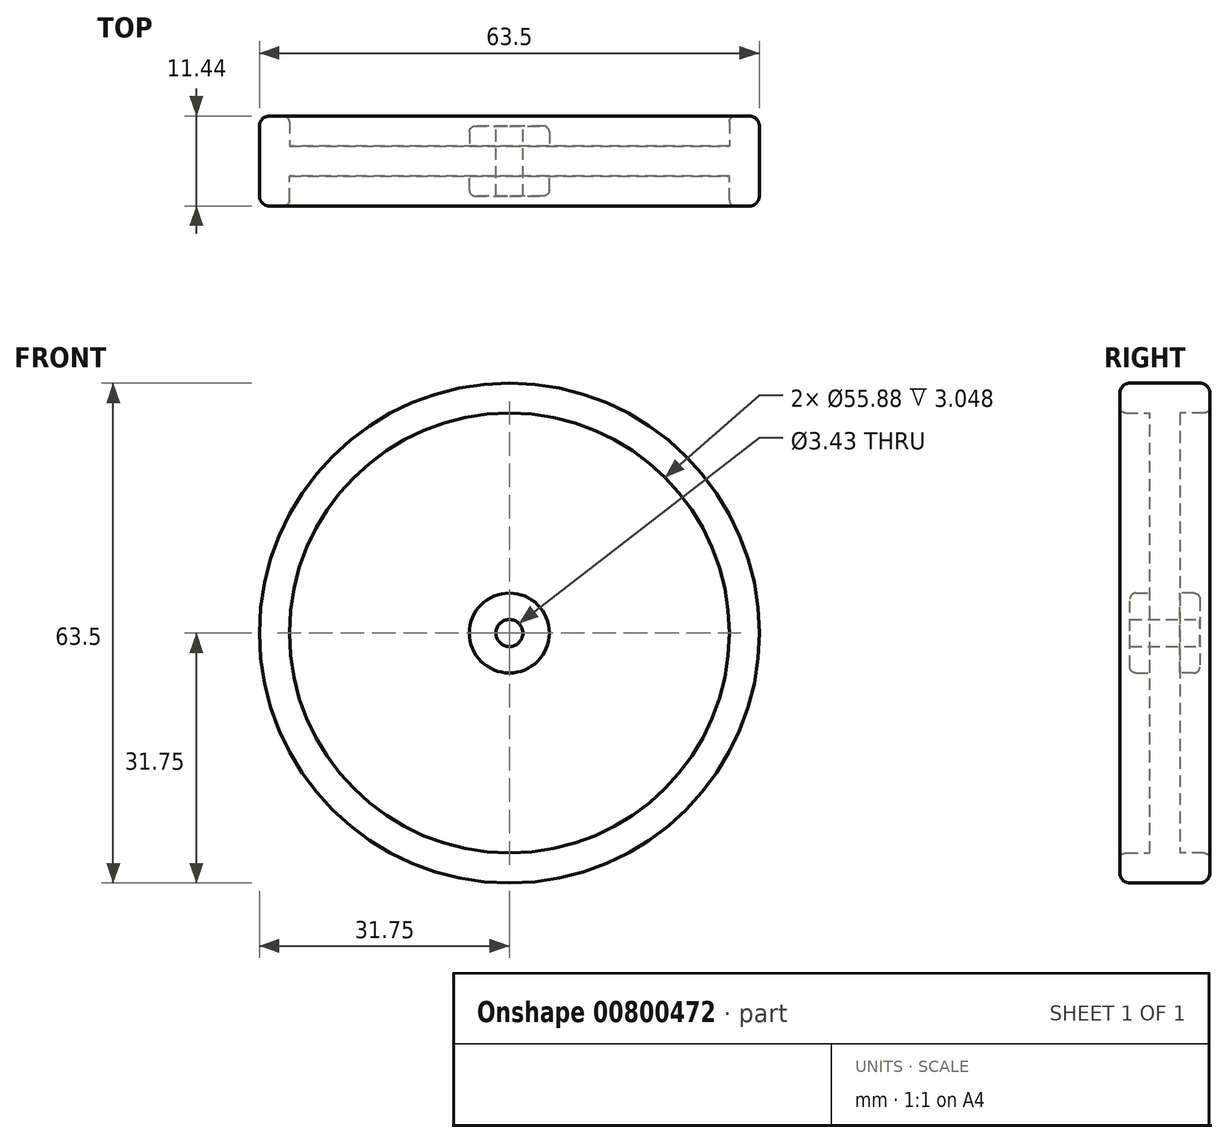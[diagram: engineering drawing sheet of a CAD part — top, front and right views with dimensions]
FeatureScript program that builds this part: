
annotation { "Feature Type Name" : "Feature", "Feature Type Description" : "" }
export const myFeature = defineFeature(function(context is Context, id is Id, definition is map)
    precondition{}
    {
        {
            var Q0;
            Q0=qCreatedBy(makeId("Front.planeOp"),FACE);
            var sketch = newSketch(context, id + "F0", { "sketchPlane" : qUnion([Q0])});
            skCircle(sketch, "E0", {"center": v(0, 0) * mm, "radius": 31.75 * mm});
            skCircle(sketch, "E1", {"center": v(0, 0) * mm, "radius": 1.71 * mm});
            skCircle(sketch, "E2", {"center": v(0, 0) * mm, "radius": 25.4 * mm});
            skSolve(sketch);
        }
        {
            var Q0;
            Q0=makeQuery(id+"F0.imprint","IMPRINT",FACE,{"disambiguationData":[TD([[makeQuery(id+"F0.imprint","IMPRINT",EDGE,{"derivedFrom":sQuery(id+"F0.wireOp",EDGE,"E0")}),1.0]])]});
            var Q1;
            Q1=makeQuery(id+"F0.imprint","IMPRINT",FACE,{"disambiguationData":[TD([[makeQuery(id+"F0.imprint","IMPRINT",EDGE,{"derivedFrom":sQuery(id+"F0.wireOp",EDGE,"E1")}),-1.0]])]});
            extrude(context, id + "F1", {"entities" : qUnion([Q0, Q1]), "endBound" : BoundingType.SYMMETRIC, "depth" : 3.8 * mm, "offsetDistance" : 25.4 * mm});
        }
        {
            var Q0;
            Q0=makeQuery(id+"F1.opExtrude","CAP_FACE",FACE,{"disambiguationData":[OSD([sQuery(id+"F0.wireOp",EDGE,"E0"),sQuery(id+"F0.wireOp",EDGE,"E1")])],"isStart":false});
            var sketch = newSketch(context, id + "F2", { "sketchPlane" : qUnion([Q0])});
            skCircle(sketch, "E3", {"center": v(0, 0) * mm, "radius": 27.94 * mm});
            skSolve(sketch);
        }
        {
            var Q0;
            Q0=makeQuery(id+"F2.imprint","IMPRINT",FACE,{"disambiguationData":[TD([[makeQuery(id+"F2.imprint","IMPRINT",EDGE,{"derivedFrom":sQuery(id+"F2.wireOp",EDGE,"E3")}),-1.0]])]});
            extrude(context, id + "F3", {"entities" : qUnion([Q0]), "operationType" : NewBodyOperationType.ADD, "depth" : 3.8 * mm, "offsetDistance" : 25.4 * mm});
        }
        {
            var Q0;
            Q0=makeQuery(id+"F1.opExtrude","CAP_FACE",FACE,{"disambiguationData":[OSD([sQuery(id+"F0.wireOp",EDGE,"E0"),sQuery(id+"F0.wireOp",EDGE,"E1")])],"isStart":true});
            var sketch = newSketch(context, id + "F4", { "sketchPlane" : qUnion([Q0])});
            skCircle(sketch, "E4", {"center": v(0, 0) * mm, "radius": 27.94 * mm});
            skSolve(sketch);
        }
        {
            var Q0;
            Q0=makeQuery(id+"F4.imprint","IMPRINT",FACE,{"disambiguationData":[TD([[makeQuery(id+"F4.imprint","IMPRINT",EDGE,{"derivedFrom":sQuery(id+"F4.wireOp",EDGE,"E4")}),-1.0]])]});
            extrude(context, id + "F5", {"entities" : qUnion([Q0]), "operationType" : NewBodyOperationType.ADD, "depth" : 3.8 * mm, "offsetDistance" : 25.4 * mm});
        }
        {
            var Q0;
            Q0=makeQuery(id+"F1.opExtrude","CAP_FACE",FACE,{"disambiguationData":[OSD([sQuery(id+"F0.wireOp",EDGE,"E0"),sQuery(id+"F0.wireOp",EDGE,"E1")])],"isStart":false});
            var sketch = newSketch(context, id + "F6", { "sketchPlane" : qUnion([Q0])});
            skCircle(sketch, "E5", {"center": v(0, 0) * mm, "radius": 5.08 * mm});
            skSolve(sketch);
        }
        {
            var Q0;
            Q0=makeQuery(id+"F6.imprint","IMPRINT",FACE,{"disambiguationData":[TD([[makeQuery(id+"F6.imprint","IMPRINT",EDGE,{"derivedFrom":sQuery(id+"F6.wireOp",EDGE,"E5")}),1.0]])]});
            extrude(context, id + "F7", {"entities" : qUnion([Q0]), "operationType" : NewBodyOperationType.ADD, "depth" : 2.54 * mm, "offsetDistance" : 25.4 * mm});
        }
        {
            var Q0;
            Q0=makeQuery(id+"F1.opExtrude","CAP_FACE",FACE,{"disambiguationData":[OSD([sQuery(id+"F0.wireOp",EDGE,"E0"),sQuery(id+"F0.wireOp",EDGE,"E1")])],"isStart":true});
            var sketch = newSketch(context, id + "F8", { "sketchPlane" : qUnion([Q0])});
            skCircle(sketch, "E6", {"center": v(0, 0) * mm, "radius": 5.08 * mm});
            skSolve(sketch);
        }
        {
            var Q0;
            Q0=makeQuery(id+"F8.imprint","IMPRINT",FACE,{"disambiguationData":[TD([[makeQuery(id+"F8.imprint","IMPRINT",EDGE,{"derivedFrom":sQuery(id+"F8.wireOp",EDGE,"E6")}),1.0]])]});
            extrude(context, id + "F9", {"entities" : qUnion([Q0]), "operationType" : NewBodyOperationType.ADD, "depth" : 2.54 * mm, "offsetDistance" : 25.4 * mm});
        }
        {
            var Q0;
            Q0=makeQuery(id+"F5.opExtrude","CAP_EDGE",EDGE,{"disambiguationData":[OSD([sQuery(id+"F4.wireOp",EDGE,"E4")])],"isStart":false});
            var Q1;
            Q1=makeQuery(id+"F3.opExtrude","CAP_EDGE",EDGE,{"disambiguationData":[OSD([sQuery(id+"F2.wireOp",EDGE,"E3")])],"isStart":false});
            var Q2;
            Q2=makeQuery(id+"F9.opExtrude","CAP_EDGE",EDGE,{"disambiguationData":[OSD([sQuery(id+"F8.wireOp",EDGE,"E6")])],"isStart":false});
            var Q3;
            Q3=makeQuery(id+"F7.opExtrude","CAP_EDGE",EDGE,{"disambiguationData":[OSD([sQuery(id+"F6.wireOp",EDGE,"E5")])],"isStart":false});
            fillet(context, id + "F10", {"entities" : qUnion([Q0, Q1, Q2, Q3]), "radius" : 0.76 * mm, "tangentPropagation" : true, "allowEdgeOverflow" : false});
        }
        {
            var Q0;
            Q0=makeQuery(id+"F3.opExtrude","CAP_EDGE",EDGE,{"disambiguationData":[OSD([sQuery(id+"F0.wireOp",EDGE,"E0")])],"isStart":false});
            var Q1;
            Q1=makeQuery(id+"F5.opExtrude","CAP_EDGE",EDGE,{"disambiguationData":[OSD([sQuery(id+"F0.wireOp",EDGE,"E0")])],"isStart":false});
            fillet(context, id + "F11", {"entities" : qUnion([Q0, Q1]), "radius" : 1.27 * mm, "tangentPropagation" : true, "allowEdgeOverflow" : false});
        }
    });
